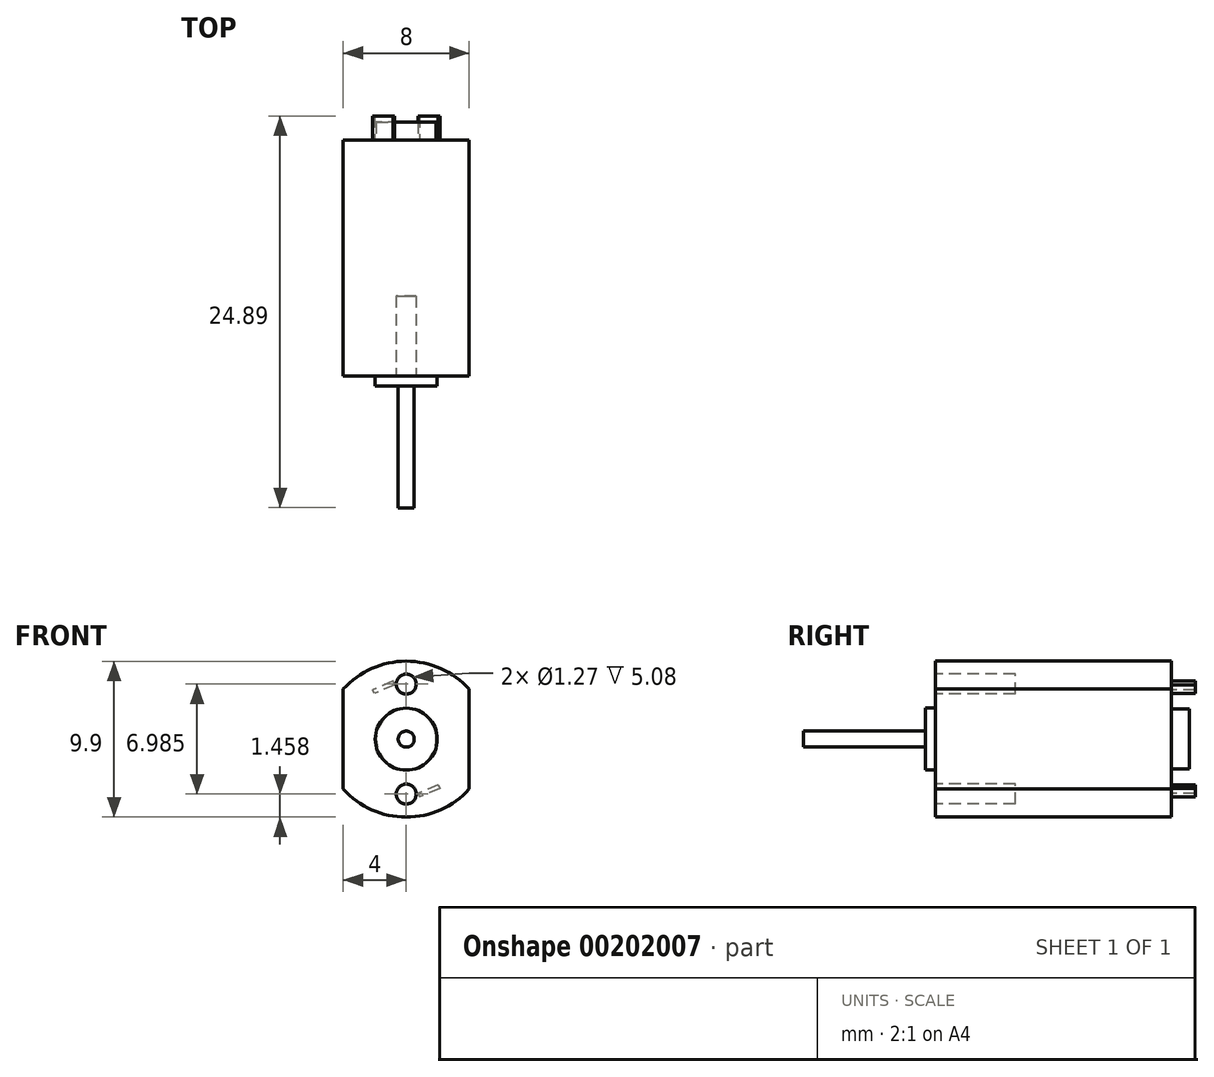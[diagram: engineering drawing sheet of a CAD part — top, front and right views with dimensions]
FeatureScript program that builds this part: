
annotation { "Feature Type Name" : "Feature", "Feature Type Description" : "" }
export const myFeature = defineFeature(function(context is Context, id is Id, definition is map)
    precondition{}
    {
        {
            var Q0;
            Q0=qCreatedBy(makeId("Front.planeOp"),FACE);
            var sketch = newSketch(context, id + "F0", { "sketchPlane" : qUnion([Q0])});
            skLineSegment(sketch, "E0.left", {"start": v(4, 3.18) * mm, "end": v(4, -3.18) * mm});
            skLineSegment(sketch, "E0.right", {"start": v(-4, 3.18) * mm, "end": v(-4, -3.18) * mm});
            skPoint(sketch, "E0.middle", {"position": v(0, 0) * mm});
            skLineSegment(sketch, "E1", {"start": v(0, 4.95) * mm, "end": v(0, -4.95) * mm, "construction": true});
            skArc(sketch, "E2", {"start": v(4, 3.18) * mm, "mid": v(0, 4.95) * mm, "end": v(-4, 3.18) * mm});
            skArc(sketch, "E3", {"start": v(-4, -3.18) * mm, "mid": v(0, -4.95) * mm, "end": v(4, -3.18) * mm});
            skSolve(sketch);
        }
        {
            var Q0;
            Q0=makeQuery(id+"F0.imprint","IMPRINT",FACE,{"disambiguationData":[TD([[makeQuery(id+"F0.imprint","IMPRINT",EDGE,{"derivedFrom":sQuery(id+"F0.wireOp",EDGE,"E0.left")}),-1.0]])]});
            extrude(context, id + "F1", {"entities" : qUnion([Q0]), "oppositeDirection" : true, "depth" : 15 * mm});
        }
        {
            var Q0;
            Q0=makeQuery(id+"F1.opExtrude","CAP_FACE",FACE,{"disambiguationData":[OSD([sQuery(id+"F0.wireOp",EDGE,"E0.left"),sQuery(id+"F0.wireOp",EDGE,"E0.right"),sQuery(id+"F0.wireOp",EDGE,"E2"),sQuery(id+"F0.wireOp",EDGE,"E3")])],"isStart":true});
            var sketch = newSketch(context, id + "F2", { "sketchPlane" : qUnion([Q0])});
            skCircle(sketch, "E4", {"center": v(0, 0) * mm, "radius": 0.5 * mm});
            skSolve(sketch);
        }
        {
            var Q0;
            Q0=makeQuery(id+"F2.imprint","IMPRINT",FACE,{"disambiguationData":[TD([[makeQuery(id+"F2.imprint","IMPRINT",EDGE,{"derivedFrom":sQuery(id+"F2.wireOp",EDGE,"E4")}),1.0]])]});
            extrude(context, id + "F3", {"entities" : qUnion([Q0]), "operationType" : NewBodyOperationType.ADD, "depth" : 8.38 * mm});
        }
        {
            var Q0;
            Q0=makeQuery(id+"F1.opExtrude","CAP_FACE",FACE,{"disambiguationData":[OSD([sQuery(id+"F0.wireOp",EDGE,"E0.left"),sQuery(id+"F0.wireOp",EDGE,"E0.right"),sQuery(id+"F0.wireOp",EDGE,"E2"),sQuery(id+"F0.wireOp",EDGE,"E3")])],"isStart":true});
            var sketch = newSketch(context, id + "F4", { "sketchPlane" : qUnion([Q0])});
            skCircle(sketch, "E5", {"center": v(0, 3.5) * mm, "radius": 0.64 * mm});
            skLineSegment(sketch, "E6", {"start": v(0, 3.5) * mm, "end": v(0, -3.5) * mm, "construction": true});
            skCircle(sketch, "E7", {"center": v(0, -3.5) * mm, "radius": 0.64 * mm});
            skSolve(sketch);
        }
        {
            var Q0;
            Q0=makeQuery(id+"F4.imprint","IMPRINT",FACE,{"disambiguationData":[TD([[makeQuery(id+"F4.imprint","IMPRINT",EDGE,{"derivedFrom":sQuery(id+"F4.wireOp",EDGE,"E5")}),1.0]])]});
            var Q1;
            Q1=makeQuery(id+"F4.imprint","IMPRINT",FACE,{"disambiguationData":[TD([[makeQuery(id+"F4.imprint","IMPRINT",EDGE,{"derivedFrom":sQuery(id+"F4.wireOp",EDGE,"E7")}),1.0]])]});
            extrude(context, id + "F5", {"entities" : qUnion([Q0, Q1]), "operationType" : NewBodyOperationType.REMOVE, "oppositeDirection" : true, "depth" : 5.08 * mm});
        }
        {
            var Q0;
            Q0=makeQuery(id+"F1.opExtrude","CAP_FACE",FACE,{"disambiguationData":[OSD([sQuery(id+"F0.wireOp",EDGE,"E0.left"),sQuery(id+"F0.wireOp",EDGE,"E0.right"),sQuery(id+"F0.wireOp",EDGE,"E2"),sQuery(id+"F0.wireOp",EDGE,"E3")])],"isStart":true});
            var sketch = newSketch(context, id + "F6", { "sketchPlane" : qUnion([Q0])});
            skCircle(sketch, "E8", {"center": v(0, 0) * mm, "radius": 1.97 * mm});
            skSolve(sketch);
        }
        {
            var Q0;
            Q0=makeQuery(id+"F6.imprint","IMPRINT",FACE,{"disambiguationData":[TD([[makeQuery(id+"F6.imprint","IMPRINT",EDGE,{"derivedFrom":sQuery(id+"F6.wireOp",EDGE,"E8")}),1.0]])]});
            extrude(context, id + "F7", {"entities" : qUnion([Q0]), "operationType" : NewBodyOperationType.ADD, "depth" : 0.64 * mm});
        }
        {
            var Q0;
            Q0=makeQuery(id+"F1.opExtrude","CAP_FACE",FACE,{"disambiguationData":[OSD([sQuery(id+"F0.wireOp",EDGE,"E0.left"),sQuery(id+"F0.wireOp",EDGE,"E0.right"),sQuery(id+"F0.wireOp",EDGE,"E2"),sQuery(id+"F0.wireOp",EDGE,"E3")])],"isStart":false});
            var sketch = newSketch(context, id + "F8", { "sketchPlane" : qUnion([Q0])});
            skCircle(sketch, "E9", {"center": v(0, 0) * mm, "radius": 1.9 * mm});
            skSolve(sketch);
        }
        {
            var Q0;
            Q0=makeQuery(id+"F8.imprint","IMPRINT",FACE,{"disambiguationData":[TD([[makeQuery(id+"F8.imprint","IMPRINT",EDGE,{"derivedFrom":sQuery(id+"F8.wireOp",EDGE,"E9")}),1.0]])]});
            extrude(context, id + "F9", {"entities" : qUnion([Q0]), "operationType" : NewBodyOperationType.ADD, "depth" : 1.14 * mm});
        }
        {
            var Q0;
            Q0=makeQuery(id+"F1.opExtrude","CAP_FACE",FACE,{"disambiguationData":[OSD([sQuery(id+"F0.wireOp",EDGE,"E0.left"),sQuery(id+"F0.wireOp",EDGE,"E0.right"),sQuery(id+"F0.wireOp",EDGE,"E2"),sQuery(id+"F0.wireOp",EDGE,"E3")])],"isStart":false});
            var sketch = newSketch(context, id + "F10", { "sketchPlane" : qUnion([Q0])});
            skLineSegment(sketch, "E10", {"start": v(-2, -4.57) * mm, "end": v(2, 4.57) * mm, "construction": true});
            skLineSegment(sketch, "E11", {"start": v(0, -5.6) * mm, "end": v(-4, -5.6) * mm, "construction": true});
            skLineSegment(sketch, "E12", {"start": v(-2, -3.54) * mm, "end": v(-2, -5.6) * mm, "construction": true});
            skLineSegment(sketch, "E13", {"start": v(-2.13, -3.12) * mm, "end": v(-0.85, -3.68) * mm});
            skLineSegment(sketch, "E14", {"start": v(-1.5, -3.4) * mm, "end": v(-2, -4.57) * mm, "construction": true});
            skLineSegment(sketch, "E15.0", {"start": v(-2.03, -2.9) * mm, "end": v(-0.75, -3.45) * mm});
            skLineSegment(sketch, "E16", {"start": v(-0.75, -3.45) * mm, "end": v(-0.85, -3.68) * mm});
            skLineSegment(sketch, "E17", {"start": v(-2.03, -2.9) * mm, "end": v(-2.13, -3.12) * mm});
            skLineSegment(sketch, "E18", {"start": v(-5.18, 2.27) * mm, "end": v(4.66, -2.04) * mm, "construction": true});
            skLineSegment(sketch, "E19.MirrorCS", {"start": v(0.75, 3.45) * mm, "end": v(0.85, 3.68) * mm});
            skLineSegment(sketch, "E20.MirrorCS", {"start": v(2.03, 2.9) * mm, "end": v(2.13, 3.12) * mm});
            skLineSegment(sketch, "E21.MirrorCS", {"start": v(0.85, 3.68) * mm, "end": v(2.13, 3.12) * mm});
            skLineSegment(sketch, "E22.MirrorCS", {"start": v(0.75, 3.45) * mm, "end": v(2.03, 2.9) * mm});
            skSolve(sketch);
        }
        {
            var Q0;
            Q0=makeQuery(id+"F10.imprint","IMPRINT",FACE,{"disambiguationData":[TD([[makeQuery(id+"F10.imprint","IMPRINT",EDGE,{"derivedFrom":sQuery(id+"F10.wireOp",EDGE,"E13")}),1.0]])]});
            var Q1;
            Q1=makeQuery(id+"F10.imprint","IMPRINT",FACE,{"disambiguationData":[TD([[makeQuery(id+"F10.imprint","IMPRINT",EDGE,{"derivedFrom":sQuery(id+"F10.wireOp",EDGE,"E19.MirrorCS")}),-1.0]])]});
            extrude(context, id + "F11", {"entities" : qUnion([Q0, Q1]), "operationType" : NewBodyOperationType.ADD, "depth" : 1.52 * mm});
        }
    });
